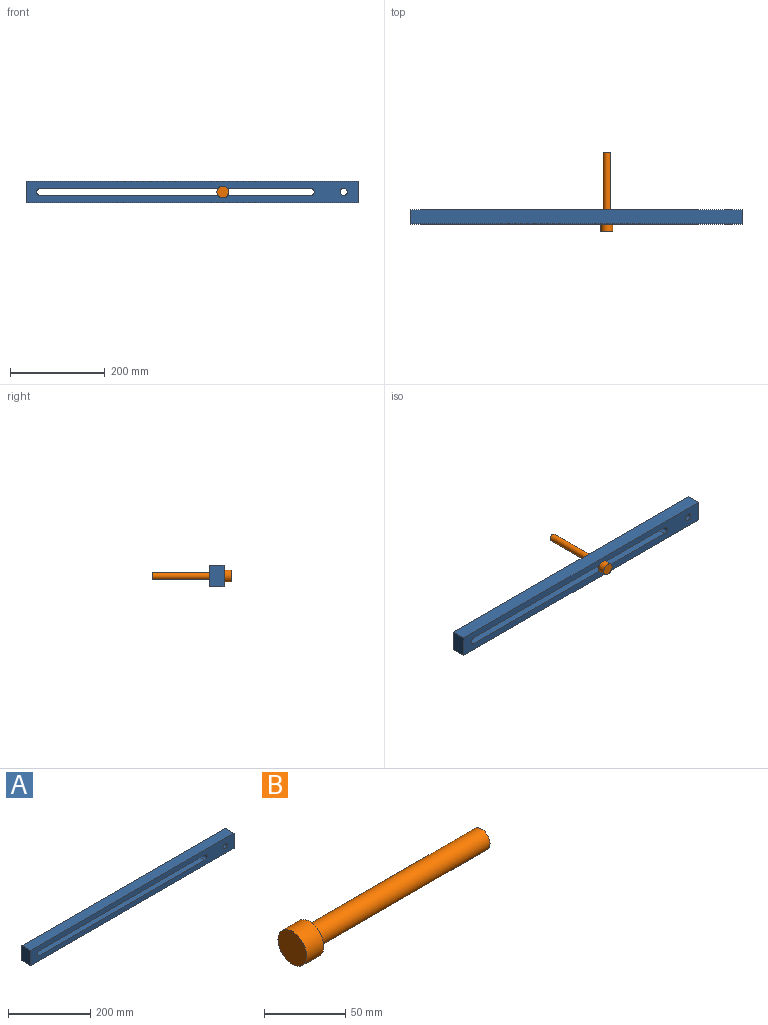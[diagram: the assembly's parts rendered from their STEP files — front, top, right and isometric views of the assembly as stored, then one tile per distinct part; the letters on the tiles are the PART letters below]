
ASSEMBLY  parts=2 mates=1
PART A: 11 faces, bbox 700x30x45 mm
  f0: plane 700x30mm, normal (0,0,1), area 21000mm2, adj f1,f8,f9,f10
  f1: plane 45x30mm, normal (-1,0,0), area 1350mm2, adj f0,f2,f9,f10
  f2: plane 700x30mm, normal (0,0,-1), area 21000mm2, adj f1,f8,f9,f10
  f3: plane 570x30mm, normal (0,0,-1), area 17100mm2, adj f4,f6,f9,f10
  f4: cylinder r=7.5mm len=30mm, axis (0,1,0), area 706.9mm2, adj f3,f5,f9,f10
  f5: plane 570x30mm, normal (0,0,1), area 17100mm2, adj f4,f6,f9,f10
  f6: cylinder r=7.5mm len=30mm, axis (0,1,0), area 706.9mm2, adj f3,f5,f9,f10
  f7: cylinder r=7.5mm len=30mm, axis (0,1,0), area 1413.7mm2, adj f9,f10
  f8: plane 45x30mm, normal (1,0,0), area 1350mm2, adj f0,f2,f9,f10
  f9: plane 700x45mm, normal (0,-1,0), area 22596.6mm2, adj f0,f1,f2,f3,f4,f5,f6,f7
  f10: plane 700x45mm, normal (0,1,0), area 22596.6mm2, adj f0,f1,f2,f3,f4,f5,f6,f7
PART B: 5 faces, bbox 165x25x25 mm
  f0: cylinder r=12.5mm len=25mm, axis (-1,0,0), area 1178.1mm2, adj f1,f2
  f1: plane 25x25mm, normal (1,0,0), area 314.2mm2, adj f0,f3
  f2: plane 25x25mm, normal (-1,0,0), area 490.9mm2, adj f0
  f3: cylinder r=7.5mm len=150mm, axis (-1,0,0), area 7068.6mm2, adj f1,f4
  f4: plane 15x15mm, normal (1,0,0), area 176.7mm2, adj f3
PLACE A at identity fixed
PLACE B rot(axis=(-0.49,-0.49,0.73),108.1deg) t=(-255,-30,0)mm
MATE pin_slot B.f0 <-> A.f9  axis (0,1,0) through (-255,-15,0)mm
